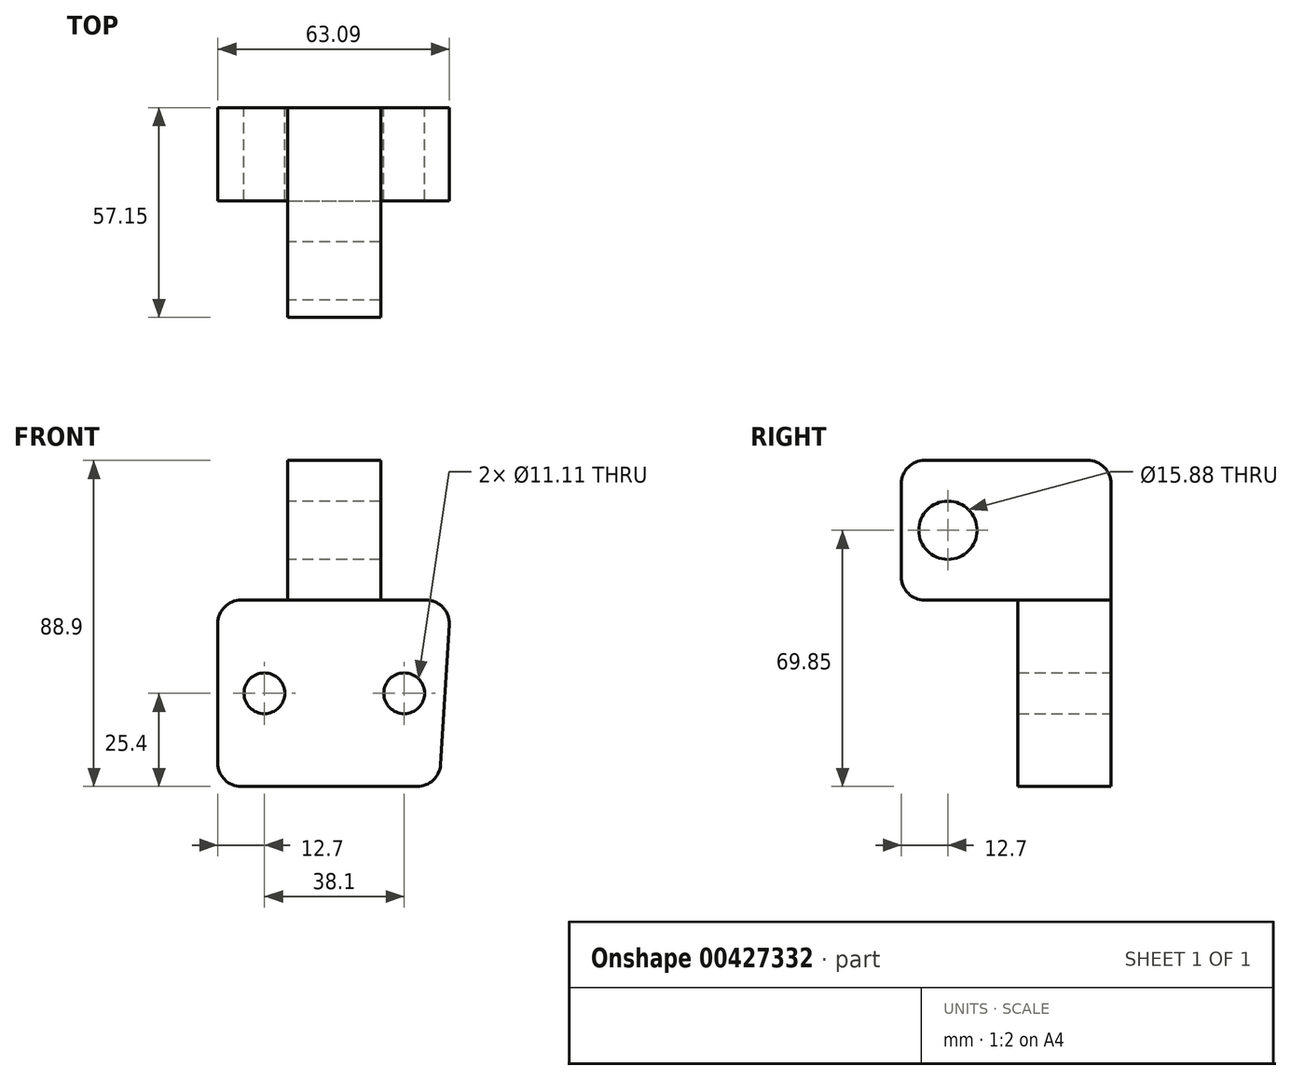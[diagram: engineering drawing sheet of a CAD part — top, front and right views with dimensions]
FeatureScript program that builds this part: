
annotation { "Feature Type Name" : "Feature", "Feature Type Description" : "" }
export const myFeature = defineFeature(function(context is Context, id is Id, definition is map)
    precondition{}
    {
        {
            var Q0;
            Q0=qCreatedBy(makeId("Front.planeOp"),FACE);
            var sketch = newSketch(context, id + "F0", { "sketchPlane" : qUnion([Q0])});
            skLineSegment(sketch, "E0", {"start": v(6.35, 0) * mm, "end": v(54.36, 0) * mm});
            skLineSegment(sketch, "E1", {"start": v(0, 6.35) * mm, "end": v(0, 44.45) * mm});
            skLineSegment(sketch, "E2", {"start": v(6.35, 50.8) * mm, "end": v(56.74, 50.8) * mm});
            skLineSegment(sketch, "E3", {"start": v(63.08, 44.05) * mm, "end": v(60.7, 5.95) * mm});
            skPoint(sketch, "E4.visualSharp", {"position": v(0, 50.8) * mm});
            skArc(sketch, "E4.filletArc", {"start": v(6.35, 50.8) * mm, "mid": v(1.86, 48.94) * mm, "end": v(0, 44.45) * mm});
            skPoint(sketch, "E5.visualSharp", {"position": v(63.5, 50.8) * mm});
            skArc(sketch, "E5.filletArc", {"start": v(63.08, 44.05) * mm, "mid": v(61.37, 48.8) * mm, "end": v(56.74, 50.8) * mm});
            skPoint(sketch, "E6.visualSharp", {"position": v(60.33, 0) * mm});
            skArc(sketch, "E6.filletArc", {"start": v(54.36, 0) * mm, "mid": v(58.7, 1.72) * mm, "end": v(60.7, 5.95) * mm});
            skPoint(sketch, "E7.visualSharp", {"position": v(0, 0) * mm});
            skArc(sketch, "E7.filletArc", {"start": v(0, 6.35) * mm, "mid": v(1.86, 1.86) * mm, "end": v(6.35, 0) * mm});
            skCircle(sketch, "E8", {"center": v(12.7, 25.4) * mm, "radius": 5.56 * mm});
            skCircle(sketch, "E9", {"center": v(50.8, 25.4) * mm, "radius": 5.56 * mm});
            skSolve(sketch);
        }
        {
            var Q0;
            Q0 = qSketchRegion(id + "F0", true);
            extrude(context, id + "F1", {"entities" : qUnion([Q0]), "depth" : 25.4 * mm});
        }
        {
            var Q0;
            Q0=makeQuery(id+"F1.opExtrude","SWEPT_FACE",FACE,{"disambiguationData":[OSD([sQuery(id+"F0.wireOp",EDGE,"E2")])]});
            var sketch = newSketch(context, id + "F2", { "sketchPlane" : qUnion([Q0])});
            skLineSegment(sketch, "E10.bottom", {"start": v(19.05, 0) * mm, "end": v(44.45, 0) * mm});
            skLineSegment(sketch, "E10.top", {"start": v(19.05, -57.15) * mm, "end": v(44.45, -57.15) * mm});
            skLineSegment(sketch, "E10.left", {"start": v(19.05, 0) * mm, "end": v(19.05, -57.15) * mm});
            skLineSegment(sketch, "E10.right", {"start": v(44.45, 0) * mm, "end": v(44.45, -57.15) * mm});
            skSolve(sketch);
        }
        {
            var Q0;
            Q0 = qSketchRegion(id + "F2", true);
            extrude(context, id + "F3", {"entities" : qUnion([Q0]), "operationType" : NewBodyOperationType.ADD, "depth" : 38.1 * mm});
        }
        {
            var Q0;
            Q0=makeQuery(id+"F3.opExtrude","CAP_EDGE",EDGE,{"disambiguationData":[OSD([sQuery(id+"F2.wireOp",EDGE,"E10.top")])],"isStart":false});
            var Q1;
            Q1=makeQuery(id+"F3.opExtrude","CAP_EDGE",EDGE,{"disambiguationData":[OSD([sQuery(id+"F2.wireOp",EDGE,"E10.top")])],"isStart":true});
            var Q2;
            Q2=makeQuery(id+"F3.opExtrude","CAP_EDGE",EDGE,{"disambiguationData":[OSD([sQuery(id+"F2.wireOp",EDGE,"E10.bottom")])],"isStart":false});
            fillet(context, id + "F4", {"entities" : qUnion([Q0, Q1, Q2]), "radius" : 6.35 * mm, "tangentPropagation" : true, "allowEdgeOverflow" : false});
        }
        {
            var Q0;
            Q0=makeQuery(id+"F3.opExtrude","SWEPT_FACE",FACE,{"disambiguationData":[OSD([sQuery(id+"F2.wireOp",EDGE,"E10.left")])]});
            var sketch = newSketch(context, id + "F5", { "sketchPlane" : qUnion([Q0])});
            skCircle(sketch, "E11", {"center": v(44.45, 69.85) * mm, "radius": 7.94 * mm});
            skSolve(sketch);
        }
        {
            var Q0;
            Q0 = qSketchRegion(id + "F5", true);
            extrude(context, id + "F6", {"entities" : qUnion([Q0]), "operationType" : NewBodyOperationType.REMOVE, "oppositeDirection" : true, "depth" : 25.4 * mm});
        }
    });
